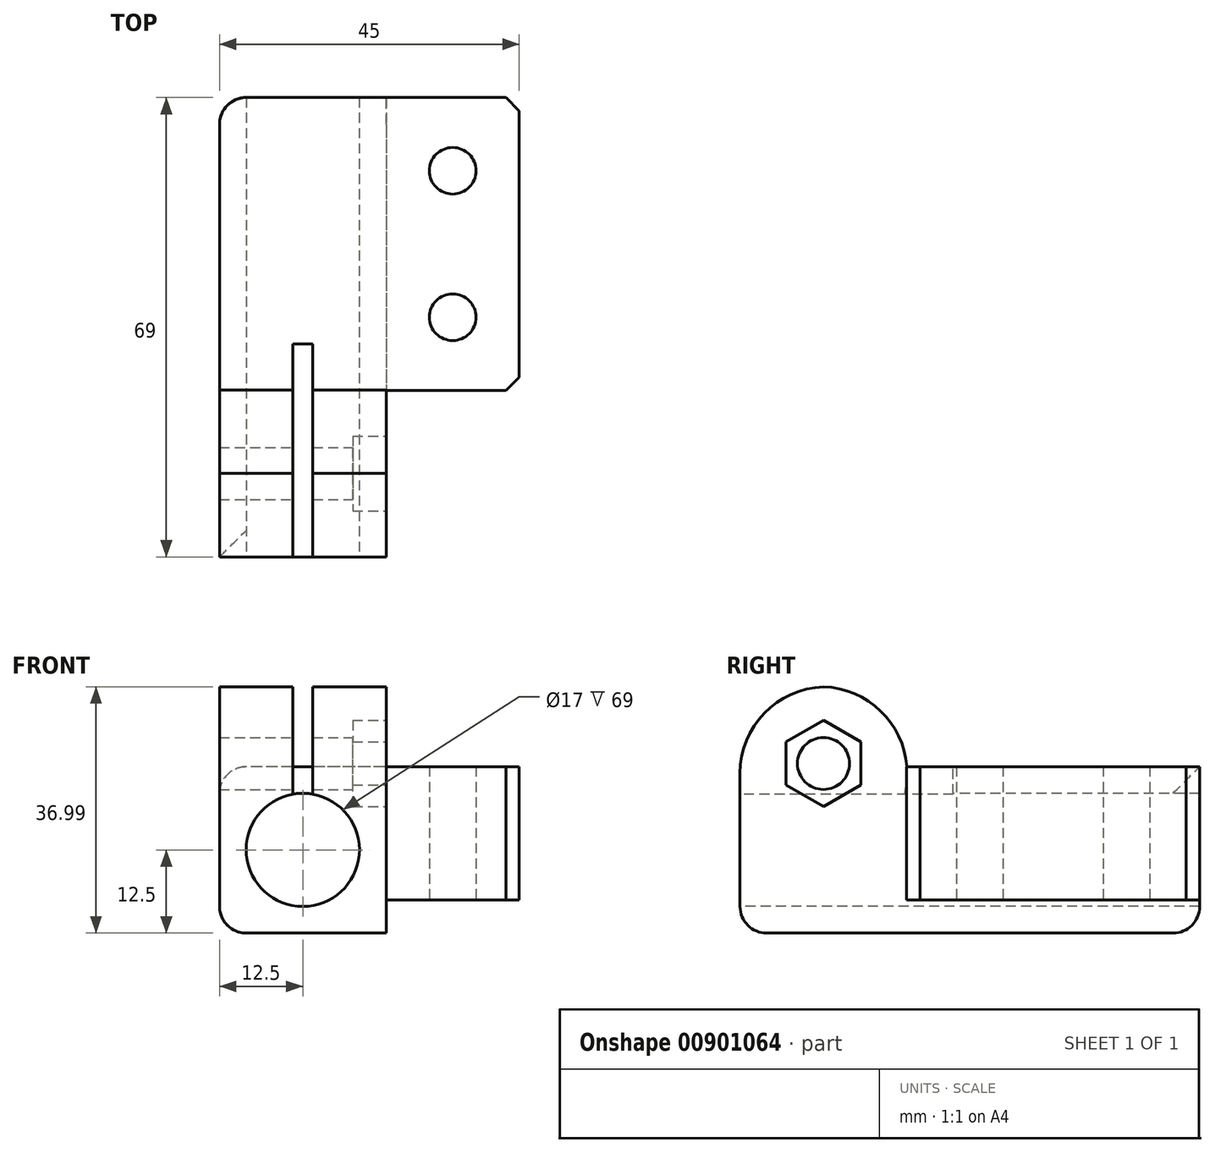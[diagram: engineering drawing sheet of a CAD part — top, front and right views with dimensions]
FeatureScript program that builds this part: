
annotation { "Feature Type Name" : "Feature", "Feature Type Description" : "" }
export const myFeature = defineFeature(function(context is Context, id is Id, definition is map)
    precondition{}
    {
        {
            var Q0;
            Q0=qCreatedBy(makeId("Top.planeOp"),FACE);
            var sketch = newSketch(context, id + "F0", { "sketchPlane" : qUnion([Q0])});
            skLineSegment(sketch, "E0.bottom", {"start": v(12.5, -22) * mm, "end": v(-12.5, -22) * mm});
            skLineSegment(sketch, "E0.top", {"start": v(12.5, 22) * mm, "end": v(-12.5, 22) * mm});
            skLineSegment(sketch, "E0.right", {"start": v(-12.5, -22) * mm, "end": v(-12.5, 22) * mm});
            skPoint(sketch, "E0.middle", {"position": v(0, 0) * mm});
            skLineSegment(sketch, "E1", {"start": v(12.5, 22) * mm, "end": v(12.5, -22) * mm});
            skLineSegment(sketch, "E2", {"start": v(12.5, -22) * mm, "end": v(32.5, -22) * mm});
            skLineSegment(sketch, "E3", {"start": v(32.5, -22) * mm, "end": v(32.5, 22) * mm});
            skLineSegment(sketch, "E4", {"start": v(32.5, 22) * mm, "end": v(12.5, 22) * mm});
            skCircle(sketch, "E5", {"center": v(22.5, 11) * mm, "radius": 3.5 * mm});
            skCircle(sketch, "E6", {"center": v(22.5, -11) * mm, "radius": 3.5 * mm});
            skLineSegment(sketch, "E7", {"start": v(-12.5, -22) * mm, "end": v(-12.5, -47) * mm});
            skLineSegment(sketch, "E8", {"start": v(-12.5, -47) * mm, "end": v(12.5, -47) * mm});
            skLineSegment(sketch, "E9", {"start": v(12.5, -47) * mm, "end": v(12.5, -22) * mm});
            skPoint(sketch, "E10.middle", {"position": v(0, -34.5) * mm});
            skPoint(sketch, "E10.middle.positionSnap0", {"position": v(12.5, -34.5) * mm});
            skPoint(sketch, "E10.centerSnap0", {"position": v(12.5, -34.5) * mm});
            skSolve(sketch);
        }
        {
            var Q0;
            Q0=makeQuery(id+"F0.imprint","IMPRINT",FACE,{"disambiguationData":[TD([[makeQuery(id+"F0.imprint","IMPRINT",EDGE,{"derivedFrom":sQuery(id+"F0.wireOp",EDGE,"E0.bottom")}),-1.0]])]});
            var Q1;
            Q1=makeQuery(id+"F0.imprint","IMPRINT",FACE,{"disambiguationData":[TD([[makeQuery(id+"F0.imprint","IMPRINT",EDGE,{"derivedFrom":sQuery(id+"F0.wireOp",EDGE,"E0.bottom")}),1.0]])]});
            extrude(context, id + "F1", {"entities" : qUnion([Q0, Q1]), "depth" : 25 * mm, "offsetDistance" : 25 * mm});
        }
        {
            var Q0;
            Q0=makeQuery(id+"F0.imprint","IMPRINT",FACE,{"disambiguationData":[TD([[makeQuery(id+"F0.imprint","IMPRINT",EDGE,{"derivedFrom":sQuery(id+"F0.wireOp",EDGE,"E1")}),1.0]])]});
            var Q1;
            Q1=makeQuery(id+"F0.imprint","IMPRINT",FACE,{"disambiguationData":[TD([[makeQuery(id+"F0.imprint","IMPRINT",EDGE,{"derivedFrom":sQuery(id+"F0.wireOp",EDGE,"fSMG0Yw6-hnwn-Rwnt-exVP-JI2tHro1bWqK")}),-1.0]])]});
            var Q2;
            Q2=makeQuery(id+"F0.imprint","IMPRINT",FACE,{"disambiguationData":[TD([[makeQuery(id+"F0.imprint","IMPRINT",EDGE,{"derivedFrom":sQuery(id+"F0.wireOp",EDGE,"jervV3UO-4z5F-xtz5-7L9T-9r2oX97e2wMv")}),-1.0]])]});
            extrude(context, id + "F2", {"entities" : qUnion([Q0, Q1, Q2]), "operationType" : NewBodyOperationType.ADD, "depth" : 25 * mm, "offsetDistance" : 25 * mm});
        }
        {
            var Q0;
            Q0=makeQuery(id+"F1.opExtrude","SWEPT_FACE",FACE,{"disambiguationData":[OSD([sQuery(id+"F0.wireOp",EDGE,"E8")])]});
            var sketch = newSketch(context, id + "F3", { "sketchPlane" : qUnion([Q0])});
            skCircle(sketch, "E11", {"center": v(0, 12.5) * mm, "radius": 8.5 * mm});
            skPoint(sketch, "E11.centerSnap0", {"position": v(0, 25) * mm});
            skPoint(sketch, "E11.centerSnap1", {"position": v(-12.5, 12.5) * mm});
            skSolve(sketch);
        }
        {
            var Q0;
            Q0=makeQuery(id+"F3.imprint","IMPRINT",FACE,{"disambiguationData":[TD([[makeQuery(id+"F3.imprint","IMPRINT",EDGE,{"derivedFrom":sQuery(id+"F3.wireOp",EDGE,"E11")}),1.0]])]});
            extrude(context, id + "F4", {"entities" : qUnion([Q0]), "operationType" : NewBodyOperationType.REMOVE, "endBound" : BoundingType.THROUGH_ALL, "oppositeDirection" : true, "depth" : 25 * mm, "offsetDistance" : 25 * mm});
        }
        {
            var Q0;
            Q0=makeQuery(id+"F1.opExtrude","CAP_FACE",FACE,{"disambiguationData":[OSD([sQuery(id+"F0.wireOp",EDGE,"E0.top"),sQuery(id+"F0.wireOp",EDGE,"E0.right"),sQuery(id+"F0.wireOp",EDGE,"E1"),sQuery(id+"F0.wireOp",EDGE,"E7"),sQuery(id+"F0.wireOp",EDGE,"E8"),sQuery(id+"F0.wireOp",EDGE,"E9")])],"isStart":false});
            var sketch = newSketch(context, id + "F5", { "sketchPlane" : qUnion([Q0])});
            skLineSegment(sketch, "E12", {"start": v(12.5, -21.95) * mm, "end": v(-12.5, -21.95) * mm});
            skLineSegment(sketch, "E13.bottom", {"start": v(-12.5, -21.95) * mm, "end": v(-1.5, -21.95) * mm});
            skLineSegment(sketch, "E13.top", {"start": v(-12.5, -47) * mm, "end": v(-1.5, -47) * mm});
            skLineSegment(sketch, "E13.left", {"start": v(-12.5, -21.95) * mm, "end": v(-12.5, -47) * mm});
            skLineSegment(sketch, "E14.bottom", {"start": v(12.5, -21.95) * mm, "end": v(1.5, -21.95) * mm});
            skLineSegment(sketch, "E14.top", {"start": v(12.5, -47) * mm, "end": v(1.5, -47) * mm});
            skLineSegment(sketch, "E14.left", {"start": v(12.5, -21.95) * mm, "end": v(12.5, -47) * mm});
            skLineSegment(sketch, "E15.bottom", {"start": v(1.5, -47) * mm, "end": v(-1.5, -47) * mm});
            skLineSegment(sketch, "E15.top", {"start": v(1.5, -15) * mm, "end": v(-1.5, -15) * mm});
            skLineSegment(sketch, "E15.left", {"start": v(1.5, -47) * mm, "end": v(1.5, -15) * mm});
            skLineSegment(sketch, "E15.right", {"start": v(-1.5, -47) * mm, "end": v(-1.5, -15) * mm});
            skSolve(sketch);
        }
        {
            var Q0;
            {var subQ4=sQuery(id+"F5.wireOp",EDGE,"E13.top");Q0=makeQuery(id+"F5.imprint","IMPRINT",FACE,{"disambiguationData":[TD([[makeQuery(id+"F5.imprint","IMPRINT",EDGE,{"derivedFrom":subQ4}),1.0]])]});}
            var Q1;
            {var subQ1=sQuery(id+"F5.wireOp",EDGE,"E14.top");Q1=makeQuery(id+"F5.imprint","IMPRINT",FACE,{"disambiguationData":[TD([[makeQuery(id+"F5.imprint","IMPRINT",EDGE,{"derivedFrom":subQ1}),1.0]])]});}
            extrude(context, id + "F6", {"entities" : qUnion([Q0, Q1]), "operationType" : NewBodyOperationType.ADD, "depth" : 12 * mm, "offsetDistance" : 25 * mm});
        }
        {
            var Q0;
            {var subQ5=sQuery(id+"F5.wireOp",EDGE,"E15.bottom");Q0=makeQuery(id+"F5.imprint","IMPRINT",FACE,{"disambiguationData":[TD([[makeQuery(id+"F5.imprint","IMPRINT",EDGE,{"derivedFrom":subQ5}),1.0]])]});}
            var Q1;
            {var subQ5=sQuery(id+"F5.wireOp",EDGE,"E15.top");Q1=makeQuery(id+"F5.imprint","IMPRINT",FACE,{"disambiguationData":[TD([[makeQuery(id+"F5.imprint","IMPRINT",EDGE,{"derivedFrom":subQ5}),1.0]])]});}
            extrude(context, id + "F7", {"entities" : qUnion([Q0, Q1]), "operationType" : NewBodyOperationType.REMOVE, "endBound" : BoundingType.UP_TO_NEXT, "oppositeDirection" : true, "depth" : 25 * mm, "offsetDistance" : 25 * mm});
        }
        {
            var Q0;
            Q0=makeQuery(id+"F6.boolean.opBoolean","MERGE",FACE,{"derivedFrom":[makeQuery(id+"F1.opExtrude","SWEPT_FACE",FACE,{"disambiguationData":[OSD([sQuery(id+"F0.wireOp",EDGE,"E1"),sQuery(id+"F0.wireOp",EDGE,"E9")])]}),makeQuery(id+"F6.opExtrude","SWEPT_FACE",FACE,{"disambiguationData":[OSD([sQuery(id+"F5.wireOp",EDGE,"E14.left")])]})]});
            var sketch = newSketch(context, id + "F8", { "sketchPlane" : qUnion([Q0])});
            skPoint(sketch, "E16.centerSnap1", {"position": v(-34.48, 37) * mm});
            skCircle(sketch, "E17", {"center": v(-34.48, 25.47) * mm, "radius": 3.9 * mm});
            skCircle(sketch, "E18.cCircle", {"center": v(-34.48, 25.47) * mm, "radius": 5.6 * mm, "construction": true});
            skLineSegment(sketch, "E18.0", {"start": v(-40.08, 22.24) * mm, "end": v(-40.08, 28.7) * mm});
            skLineSegment(sketch, "E18.1", {"start": v(-40.08, 28.7) * mm, "end": v(-34.48, 31.94) * mm});
            skLineSegment(sketch, "E18.2", {"start": v(-34.48, 31.94) * mm, "end": v(-28.88, 28.7) * mm});
            skLineSegment(sketch, "E18.3", {"start": v(-28.88, 28.7) * mm, "end": v(-28.88, 22.24) * mm});
            skLineSegment(sketch, "E18.4", {"start": v(-28.88, 22.24) * mm, "end": v(-34.48, 19) * mm});
            skLineSegment(sketch, "E18.5", {"start": v(-34.48, 19) * mm, "end": v(-40.08, 22.24) * mm});
            skPoint(sketch, "E18.0.midPoint", {"position": v(-40.08, 25.47) * mm});
            skSolve(sketch);
        }
        {
            var Q0;
            Q0=makeQuery(id+"F6.opExtrude","CAP_EDGE",EDGE,{"disambiguationData":[OSD([sQuery(id+"F5.wireOp",EDGE,"E13.top")])],"isStart":false});
            var Q1;
            Q1=makeQuery(id+"F6.opExtrude","CAP_EDGE",EDGE,{"disambiguationData":[OSD([sQuery(id+"F5.wireOp",EDGE,"E14.top")])],"isStart":false});
            var Q2;
            {var subQ0=sQuery(id+"F5.wireOp",EDGE,"E12");Q2=makeQuery(id+"F6.opExtrude","CAP_EDGE",EDGE,{"disambiguationData":[OSD([subQ0]),TDD([makeQuery(id+"F5.imprint","IMPRINT",EDGE,{"disambiguationData":[TD([[makeQuery(id+"F5.imprint","INTERSECT",VERTEX,{"derivedFrom":[subQ0,sQuery(id+"F5.wireOp",EDGE,"E14.left")]}),-1.0]])],"derivedFrom":subQ0})])],"isStart":false});}
            var Q3;
            {var subQ0=sQuery(id+"F5.wireOp",EDGE,"E12");Q3=makeQuery(id+"F6.opExtrude","CAP_EDGE",EDGE,{"disambiguationData":[OSD([subQ0]),TDD([makeQuery(id+"F5.imprint","IMPRINT",EDGE,{"disambiguationData":[TD([[makeQuery(id+"F5.imprint","INTERSECT",VERTEX,{"derivedFrom":[subQ0,sQuery(id+"F5.wireOp",EDGE,"E15.right")]}),-1.0]])],"derivedFrom":subQ0})])],"isStart":false});}
            fillet(context, id + "F9", {"entities" : qUnion([Q0, Q1, Q2, Q3]), "radius" : 13 * mm, "tangentPropagation" : true, "defaultsChanged" : true, "vertexSettings" : [], "allowEdgeOverflow" : false});
        }
        {
            var Q0;
            Q0=makeQuery(id+"F0.imprint","IMPRINT",FACE,{"disambiguationData":[TD([[makeQuery(id+"F0.imprint","IMPRINT",EDGE,{"derivedFrom":sQuery(id+"F0.wireOp",EDGE,"E1")}),1.0]])]});
            extrude(context, id + "F10", {"entities" : qUnion([Q0]), "operationType" : NewBodyOperationType.REMOVE, "depth" : 5 * mm, "offsetDistance" : 25 * mm});
        }
        {
            var Q0;
            Q0=makeQuery(id+"F8.imprint","IMPRINT",FACE,{"disambiguationData":[TD([[makeQuery(id+"F8.imprint","IMPRINT",EDGE,{"derivedFrom":sQuery(id+"F8.wireOp",EDGE,"E17")}),1.0]])]});
            extrude(context, id + "F11", {"entities" : qUnion([Q0]), "operationType" : NewBodyOperationType.REMOVE, "endBound" : BoundingType.THROUGH_ALL, "oppositeDirection" : true, "depth" : 25 * mm, "offsetDistance" : 25 * mm});
        }
        {
            var Q0;
            Q0=makeQuery(id+"F8.imprint","IMPRINT",FACE,{"disambiguationData":[TD([[makeQuery(id+"F8.imprint","IMPRINT",EDGE,{"derivedFrom":sQuery(id+"F8.wireOp",EDGE,"E17")}),1.0]])]});
            extrude(context, id + "F12", {"entities" : qUnion([Q0]), "operationType" : NewBodyOperationType.REMOVE, "endBound" : BoundingType.THROUGH_ALL, "oppositeDirection" : true, "depth" : 25 * mm, "offsetDistance" : 25 * mm});
        }
        {
            var Q0;
            Q0=makeQuery(id+"F8.imprint","IMPRINT",FACE,{"disambiguationData":[TD([[makeQuery(id+"F8.imprint","IMPRINT",EDGE,{"derivedFrom":sQuery(id+"F8.wireOp",EDGE,"E17")}),-1.0]])]});
            extrude(context, id + "F13", {"entities" : qUnion([Q0]), "operationType" : NewBodyOperationType.REMOVE, "oppositeDirection" : true, "depth" : 5 * mm, "offsetDistance" : 25 * mm});
        }
        {
            var Q0;
            Q0=makeQuery(id+"F1.opExtrude","CAP_EDGE",EDGE,{"disambiguationData":[OSD([sQuery(id+"F0.wireOp",EDGE,"E0.right"),sQuery(id+"F0.wireOp",EDGE,"E7")])],"isStart":true});
            var Q1;
            Q1=makeQuery(id+"F1.opExtrude","CAP_EDGE",EDGE,{"disambiguationData":[OSD([sQuery(id+"F0.wireOp",EDGE,"E8")])],"isStart":true});
            var Q2;
            Q2=makeQuery(id+"F1.opExtrude","CAP_EDGE",EDGE,{"disambiguationData":[OSD([sQuery(id+"F0.wireOp",EDGE,"E0.right"),sQuery(id+"F0.wireOp",EDGE,"E7")])],"isStart":false});
            var Q3;
            Q3=makeQuery(id+"F2.boolean.opBoolean","MERGE",EDGE,{"derivedFrom":[makeQuery(id+"F1.opExtrude","CAP_EDGE",EDGE,{"disambiguationData":[OSD([sQuery(id+"F0.wireOp",EDGE,"E0.top")])],"isStart":true}),makeQuery(id+"F2.opExtrude","CAP_EDGE",EDGE,{"disambiguationData":[OSD([sQuery(id+"F0.wireOp",EDGE,"E4")])],"isStart":true})]});
            var Q4;
            Q4=makeQuery(id+"F1.opExtrude","SWEPT_EDGE",EDGE,{"disambiguationData":[OSD([sQuery(id+"F0.wireOp",EDGE,"E0.top"),sQuery(id+"F0.wireOp",EDGE,"E0.right")])]});
            fillet(context, id + "F14", {"entities" : qUnion([Q0, Q1, Q2, Q3, Q4]), "tangentPropagation" : true, "radius" : 4 * mm, "defaultsChanged" : false, "vertexSettings" : [], "allowEdgeOverflow" : false});
        }
        {
            var Q0;
            Q0=makeQuery(id+"F2.opExtrude","SWEPT_EDGE",EDGE,{"disambiguationData":[OSD([sQuery(id+"F0.wireOp",EDGE,"E3"),sQuery(id+"F0.wireOp",EDGE,"E4")])]});
            var Q1;
            Q1=makeQuery(id+"F2.opExtrude","SWEPT_EDGE",EDGE,{"disambiguationData":[OSD([sQuery(id+"F0.wireOp",EDGE,"E2"),sQuery(id+"F0.wireOp",EDGE,"E3")])]});
            chamfer(context, id + "F15", {"entities" : qUnion([Q0, Q1]), "width" : 2 * mm, "tangentPropagation" : true});
        }
    });
